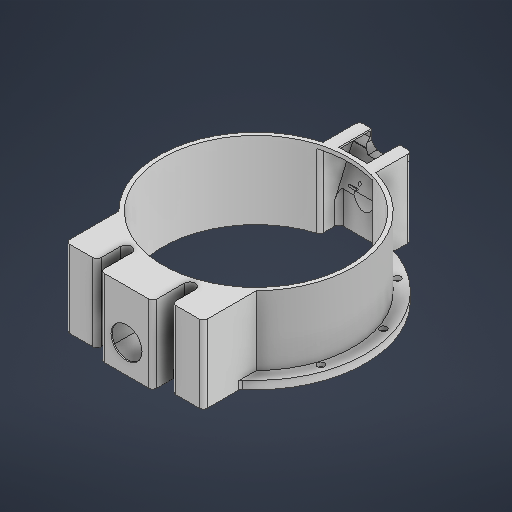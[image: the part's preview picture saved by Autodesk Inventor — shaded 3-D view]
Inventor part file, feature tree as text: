
AUTODESK INVENTOR PART (.ipt)
format: ipt  version: 2025 (Build 290162000, 162)  size: 748,032 bytes
history: native  units: in
note: dims shown in document units (in); Inventor stores cm internally (conversion verified against a paired STEP export)
features: extrude x28, sketch x20, other x3, plane x3, chamfer x3, fillet x2
ambient origin geometry x8: Origin, YZ Plane, XZ Plane, XY Plane, X Axis, Y Axis, Z Axis, Center Point
bodies: Body1 (feature_tree)
feature tree (59):
  other  "Cylinder.ipt"
  extrude  "Extrusion1"  Depth=0.3937in
  extrude  "Extrusion2"  Depth=0.3937in TaperAngle=0.0deg
  sketch  "Sketch3"  dims[d7=11.2205in d8=10.6299in]
  extrude  "Extrusion3"  Depth=10.6299in
  extrude  "Extrusion5"  Depth=0.1969in TaperAngle=0.0deg
  sketch  "Sketch6"  dims[d24=0.1969in d25=0.0in d31=0.0in d32=0.0in]
  extrude  "Extrusion6"  Depth=0.2953in
  extrude  "Extrusion7"  TaperAngle=0.0deg  [1 undecoded]
  extrude  "Extrusion8"  Depth=9.8425in
  plane  "Work Plane1"
  extrude  "Extrusion9"  Depth=10.6299in
  extrude  "Extrusion21"  Depth=0.0787in
  sketch  "Sketch18"  dims[d107=2.2047in d108=0.0in d111=3.937in d112=0.0in]
  extrude  "Extrusion22"  Depth=3.937in TaperAngle=0.0deg
  sketch  "Sketch19"  dims[d113=2.5591in d115=2.2047in d116=0.0in]
  extrude  "Extrusion23"  Depth=2.5591in TaperAngle=0.0deg
  extrude  "Extrusion27"  Depth=0.5433in
  extrude  "Extrusion31"  Depth=0.0787in
  extrude  "Extrusion32"  TaperAngle=0.0deg  [1 undecoded]
  extrude  "Extrusion33"  Depth=0.0787in
  extrude  "Extrusion34"  TaperAngle=90.0deg  [1 undecoded]
  extrude  "Extrusion40"  Depth=4.1339in TaperAngle=0.0deg
  extrude  "Extrusion42"  Depth=0.0787in
  extrude  "Extrusion43"  Depth=1.378in
  extrude  "Extrusion44"  Depth=0.1969in
  extrude  "Extrusion45"  Depth=0.1969in TaperAngle=360.0deg
  chamfer  "Chamfer8"  Distance=10.4151in
  sketch  "Sketch31"  dims[d164=1.5298in d165=0.0787in]
  extrude  "Extrusion46"  Depth=0.1969in
  extrude  "Extrusion47"  Depth=0.3937in TaperAngle=0.0deg
  plane  "Work Plane2"
  extrude  "Extrusion48"  Depth=0.5433in
  plane  "Work Plane3"
  sketch  "Sketch33"  dims[d169=2.2047in d170=0.0in d171=4.1339in d172=0.0in]
  extrude  "Extrusion49"  Depth=0.1969in
  extrude  "Extrusion50"  Depth=0.1969in
  extrude  "Extrusion51"  Depth=0.1969in
  extrude  "Extrusion52"  Depth=0.1969in
  chamfer  "Chamfer9"  Distance=3.5433in
  chamfer  "Chamfer10"  Distance=3.1693in
  fillet  "Fillet19"  Radius=3.1693in
  fillet  "Fillet20"  Radius=3.3661in
  other  "Solid12::Cylinder.ipt"
  other  "TaggingFeature1"
  sketch  "Sketch1"  dims[d0=0.3937in d2=10.2362in]
  sketch  "Sketch2"  dims[d3=0.0in d4=0.0in d5=0.3937in d6=0.0in]
  sketch  "Sketch5"  dims[d17=10.6299in d18=0.2953in]
  sketch  "Sketch7"  dims[d33=2.1654in d34=0.0in d35=9.8425in]
  sketch  "Sketch9"  dims[d36=10.6299in d46=9.065in]
  sketch  "Sketch14"  dims[d47=0.3937in d48=0.0in d88=0.0787in]
  sketch  "Sketch22"  dims[d117=0.0591in d120=0.5433in]
  sketch  "Sketch Circular Pattern3"  dims[d10=0.1969in d11=0.0in d15=0.1969in d16=0.0in]
  sketch  "Sketch28"  dims[d122=9.4488in d134=0.0787in]
  sketch  "Sketch30"  dims[d141=0.3937in d142=0.0in d159=0.0in d160=0.0in]
  sketch  "Sketch32"  dims[d166=1.8325in d167=90.0deg]
  sketch  "Sketch34"  dims[d173=1.1614in d174=0.0in d175=0.0787in]
  sketch  "Sketch35"  dims[d207=1.5157in d208=1.378in]
  sketch  "Sketch36"  dims[d209=0.2165in d210=0.3425in d211=3.937in d213=360.0deg d217=10.4151in d218=9.065in d221=0.3937in d222=0.0in d223=0.5433in d224=1.8228in d225=3.5433in d226=2.564in d227=2.7608in d228=3.5433in d231=3.1693in d232=0.0in d233=3.1693in d234=1.5846in d235=0.0in d236=0.0in d237=3.3661in d238=0.3937in d239=0.0in d240=0.0in d241=0.9843in d242=3.1496in d243=0.0in d244=1.5748in d245=0.0787in d246=0.1598in d247=0.4331in d248=0.1575in d249=0.1575in d250=0.1575in d251=0.9331in d252=0.3937in d254=0.3937in d255=0.9331in d256=0.4331in d257=0.4331in d258=2.1654in d259=0.0in d260=0.1772in d261=0.0in d262=0.315in d263=0.1666in d265=1.5871in d266=0.0in d267=1.4567in d268=0.5315in d269=-3.5433in d270=1.378in d271=1.378in d272=9.7638in d273=0.0787in d274=0.0in d275=0.6412in d276=0.0in d277=1.378in d278=0.0787in d279=1.5787in d280=0.0in d281=0.0787in d282=0.8268in d283=0.3937in d284=0.0787in d285=0.3937in d286=0.0463in d287=0.3937in d288=0.0787in d289=0.3937in d290=0.0463in d291=0.0787in d292=0.0in d293=1.378in d294=0.2756in d295=0.3076in d296=45.0deg d297=0.2756in d298=0.3076in d299=45.0deg d300=0.1969in d301=0.1969in d143=0.0197in d144=0.0344in d145=0.0197in d146=0.0344in d153=0.0in d154=0.0in d155=0.0in d156=0.0in d201=0.0197in d202=0.0344in d203=0.0197in d204=0.0344in d215=0.0197in d216=0.0344in]
note: 3 required parameter values undecoded (feature->parameter linkage not recoverable at this tier; creation-order binding heuristic only, values carry confidence <= 0.55)
